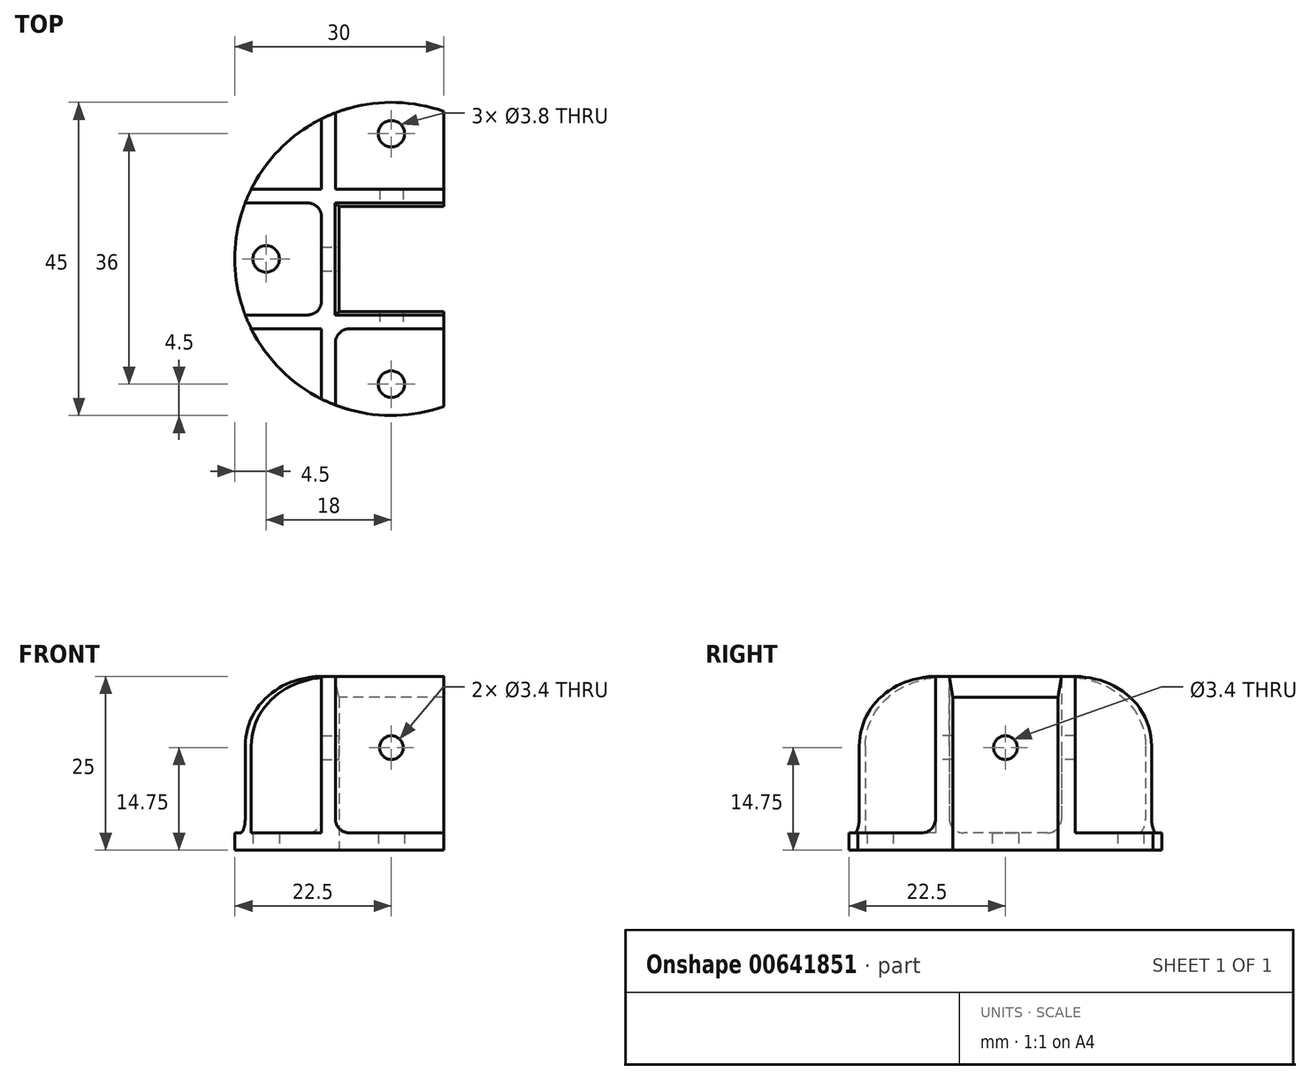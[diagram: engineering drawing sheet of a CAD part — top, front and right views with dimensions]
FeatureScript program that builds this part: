
annotation { "Feature Type Name" : "Feature", "Feature Type Description" : "" }
export const myFeature = defineFeature(function(context is Context, id is Id, definition is map)
    precondition{}
    {
        {
            var Q0;
            Q0=qCreatedBy(makeId("Top.planeOp"),FACE);
            var sketch = newSketch(context, id + "F0", { "sketchPlane" : qUnion([Q0])});
            skLineSegment(sketch, "E0.bottom", {"start": v(-7.55, 7.55) * mm, "end": v(7.55, 7.55) * mm});
            skLineSegment(sketch, "E0.top", {"start": v(-7.55, -7.55) * mm, "end": v(7.55, -7.55) * mm});
            skLineSegment(sketch, "E0.left", {"start": v(-7.55, 7.55) * mm, "end": v(-7.55, -7.55) * mm});
            skLineSegment(sketch, "E0.right", {"start": v(7.55, 7.55) * mm, "end": v(7.55, -7.55) * mm});
            skCircle(sketch, "E1", {"center": v(-18, 0) * mm, "radius": 1.9 * mm});
            skCircle(sketch, "E2", {"center": v(0, 18) * mm, "radius": 1.9 * mm});
            skCircle(sketch, "E3", {"center": v(18, 0) * mm, "radius": 1.9 * mm});
            skPoint(sketch, "E3.centerSnap0", {"position": v(10.05, 0) * mm});
            skCircle(sketch, "E4", {"center": v(0, -18) * mm, "radius": 1.9 * mm});
            skCircle(sketch, "E5", {"center": v(0, 0) * mm, "radius": 22.5 * mm});
            skSolve(sketch);
        }
        {
            var Q0;
            Q0=makeQuery(id+"F0.imprint","IMPRINT",FACE,{"disambiguationData":[TD([[makeQuery(id+"F0.imprint","IMPRINT",EDGE,{"derivedFrom":sQuery(id+"F0.wireOp",EDGE,"E0.bottom")}),1.0]])]});
            extrude(context, id + "F1", {"entities" : qUnion([Q0]), "depth" : 2.5 * mm, "offsetDistance" : 25 * mm});
        }
        {
            var Q0;
            Q0=makeQuery(id+"F1.opExtrude","CAP_FACE",FACE,{"disambiguationData":[OSD([sQuery(id+"F0.wireOp",EDGE,"E0.bottom"),sQuery(id+"F0.wireOp",EDGE,"E0.top"),sQuery(id+"F0.wireOp",EDGE,"E0.left"),sQuery(id+"F0.wireOp",EDGE,"E0.right"),sQuery(id+"F0.wireOp",EDGE,"E1"),sQuery(id+"F0.wireOp",EDGE,"E2"),sQuery(id+"F0.wireOp",EDGE,"E3"),sQuery(id+"F0.wireOp",EDGE,"E4"),sQuery(id+"F0.wireOp",EDGE,"E5")])],"isStart":false});
            var sketch = newSketch(context, id + "F2", { "sketchPlane" : qUnion([Q0])});
            skLineSegment(sketch, "E6.bottom", {"start": v(-7.55, 7.55) * mm, "end": v(7.55, 7.55) * mm});
            skLineSegment(sketch, "E6.top", {"start": v(-7.55, -7.55) * mm, "end": v(7.55, -7.55) * mm});
            skLineSegment(sketch, "E6.left", {"start": v(-7.55, 7.55) * mm, "end": v(-7.55, -7.55) * mm});
            skLineSegment(sketch, "E6.right", {"start": v(7.55, 7.55) * mm, "end": v(7.55, -7.55) * mm});
            skLineSegment(sketch, "E7.bottom", {"start": v(-10.05, 10.05) * mm, "end": v(10.05, 10.05) * mm});
            skLineSegment(sketch, "E7.top", {"start": v(-10.05, -10.05) * mm, "end": v(10.05, -10.05) * mm});
            skLineSegment(sketch, "E7.left", {"start": v(-10.05, 10.05) * mm, "end": v(-10.05, -10.05) * mm});
            skLineSegment(sketch, "E7.right", {"start": v(10.05, 10.05) * mm, "end": v(10.05, -10.05) * mm});
            skSolve(sketch);
        }
        {
            var Q0;
            Q0=makeQuery(id+"F2.imprint","IMPRINT",FACE,{"disambiguationData":[TD([[makeQuery(id+"F2.imprint","IMPRINT",EDGE,{"derivedFrom":sQuery(id+"F2.wireOp",EDGE,"E6.bottom")}),1.0]])]});
            extrude(context, id + "F3", {"entities" : qUnion([Q0]), "operationType" : NewBodyOperationType.ADD, "depth" : 22.5 * mm, "offsetDistance" : 25 * mm});
        }
        {
            var Q0;
            Q0=makeQuery(id+"F1.opExtrude","CAP_FACE",FACE,{"disambiguationData":[OSD([sQuery(id+"F0.wireOp",EDGE,"E0.bottom"),sQuery(id+"F0.wireOp",EDGE,"E0.top"),sQuery(id+"F0.wireOp",EDGE,"E0.left"),sQuery(id+"F0.wireOp",EDGE,"E0.right"),sQuery(id+"F0.wireOp",EDGE,"E1"),sQuery(id+"F0.wireOp",EDGE,"E2"),sQuery(id+"F0.wireOp",EDGE,"E3"),sQuery(id+"F0.wireOp",EDGE,"E4"),sQuery(id+"F0.wireOp",EDGE,"E5")])],"isStart":false});
            var sketch = newSketch(context, id + "F4", { "sketchPlane" : qUnion([Q0])});
            skLineSegment(sketch, "E8", {"start": v(-10.05, -10.05) * mm, "end": v(-20.13, -10.05) * mm});
            skLineSegment(sketch, "E9", {"start": v(-10.05, -10.05) * mm, "end": v(-10.05, -20.13) * mm});
            skLineSegment(sketch, "E10", {"start": v(-10.05, 10.05) * mm, "end": v(-10.05, 20.13) * mm});
            skLineSegment(sketch, "E11", {"start": v(-10.05, 10.05) * mm, "end": v(-20.13, 10.05) * mm});
            skLineSegment(sketch, "E12", {"start": v(10.05, 10.05) * mm, "end": v(10.05, 20.13) * mm});
            skLineSegment(sketch, "E13", {"start": v(10.05, 10.05) * mm, "end": v(20.13, 10.05) * mm});
            skLineSegment(sketch, "E14", {"start": v(10.05, -10.05) * mm, "end": v(20.13, -10.05) * mm});
            skLineSegment(sketch, "E15", {"start": v(10.05, -10.05) * mm, "end": v(10.05, -20.13) * mm});
            skLineSegment(sketch, "E16", {"start": v(-10.05, -10.05) * mm, "end": v(-10.05, -8.05) * mm});
            skLineSegment(sketch, "E17", {"start": v(-10.05, -8.05) * mm, "end": v(-21.01, -8.05) * mm});
            skArc(sketch, "E18", {"start": v(-20.13, 10.05) * mm, "mid": v(-20.6, 9.06) * mm, "end": v(-21.01, 8.05) * mm});
            skLineSegment(sketch, "E19", {"start": v(-10.05, -10.05) * mm, "end": v(-8.05, -10.05) * mm});
            skLineSegment(sketch, "E20", {"start": v(-8.05, -10.05) * mm, "end": v(-8.05, -21.01) * mm});
            skLineSegment(sketch, "E21", {"start": v(10.05, -10.05) * mm, "end": v(8.05, -10.05) * mm});
            skLineSegment(sketch, "E22", {"start": v(8.05, -10.05) * mm, "end": v(8.05, -21.01) * mm});
            skLineSegment(sketch, "E23", {"start": v(10.05, -10.05) * mm, "end": v(10.05, -8.05) * mm});
            skLineSegment(sketch, "E24", {"start": v(10.05, -8.05) * mm, "end": v(21.01, -8.05) * mm});
            skLineSegment(sketch, "E25", {"start": v(-10.05, 10.05) * mm, "end": v(-10.05, 8.05) * mm});
            skLineSegment(sketch, "E26", {"start": v(-10.05, 8.05) * mm, "end": v(-21.01, 8.05) * mm});
            skLineSegment(sketch, "E27", {"start": v(-10.05, 10.05) * mm, "end": v(-8.05, 10.05) * mm});
            skLineSegment(sketch, "E28", {"start": v(-8.05, 10.05) * mm, "end": v(-8.05, 21.01) * mm});
            skLineSegment(sketch, "E29", {"start": v(10.05, 10.05) * mm, "end": v(8.05, 10.05) * mm});
            skLineSegment(sketch, "E30", {"start": v(8.05, 10.05) * mm, "end": v(8.05, 21.01) * mm});
            skLineSegment(sketch, "E31", {"start": v(10.05, 10.05) * mm, "end": v(10.05, 8.05) * mm});
            skLineSegment(sketch, "E32", {"start": v(10.05, 8.05) * mm, "end": v(21.01, 8.05) * mm});
            skArc(sketch, "E33.trimOffspring", {"start": v(-8.05, 21.01) * mm, "mid": v(-9.06, 20.6) * mm, "end": v(-10.05, 20.13) * mm});
            skArc(sketch, "E34.trimOffspring", {"start": v(10.05, 20.13) * mm, "mid": v(9.06, 20.6) * mm, "end": v(8.05, 21.01) * mm});
            skArc(sketch, "E35.trimOffspring", {"start": v(21.01, 8.05) * mm, "mid": v(20.6, 9.06) * mm, "end": v(20.13, 10.05) * mm});
            skArc(sketch, "E36.trimOffspring", {"start": v(20.13, -10.05) * mm, "mid": v(20.6, -9.06) * mm, "end": v(21.01, -8.05) * mm});
            skArc(sketch, "E37.trimOffspring", {"start": v(-21.01, -8.05) * mm, "mid": v(-20.6, -9.06) * mm, "end": v(-20.13, -10.05) * mm});
            skArc(sketch, "E38.trimOffspring", {"start": v(-10.05, -20.13) * mm, "mid": v(-9.06, -20.6) * mm, "end": v(-8.05, -21.01) * mm});
            skArc(sketch, "E39.trimOffspring", {"start": v(8.05, -21.01) * mm, "mid": v(9.06, -20.6) * mm, "end": v(10.05, -20.13) * mm});
            skSolve(sketch);
        }
        {
            var Q0;
            Q0=makeQuery(id+"F4.imprint","IMPRINT",FACE,{"disambiguationData":[TD([[makeQuery(id+"F4.imprint","IMPRINT",EDGE,{"derivedFrom":sQuery(id+"F4.wireOp",EDGE,"E11")}),1.0]])]});
            var Q1;
            Q1=makeQuery(id+"F4.imprint","IMPRINT",FACE,{"disambiguationData":[TD([[makeQuery(id+"F4.imprint","IMPRINT",EDGE,{"derivedFrom":sQuery(id+"F4.wireOp",EDGE,"E8")}),-1.0]])]});
            var Q2;
            Q2=makeQuery(id+"F4.imprint","IMPRINT",FACE,{"disambiguationData":[TD([[makeQuery(id+"F4.imprint","IMPRINT",EDGE,{"derivedFrom":sQuery(id+"F4.wireOp",EDGE,"E9")}),1.0]])]});
            var Q3;
            Q3=makeQuery(id+"F4.imprint","IMPRINT",FACE,{"disambiguationData":[TD([[makeQuery(id+"F4.imprint","IMPRINT",EDGE,{"derivedFrom":sQuery(id+"F4.wireOp",EDGE,"E15")}),-1.0]])]});
            var Q4;
            Q4=makeQuery(id+"F4.imprint","IMPRINT",FACE,{"disambiguationData":[TD([[makeQuery(id+"F4.imprint","IMPRINT",EDGE,{"derivedFrom":sQuery(id+"F4.wireOp",EDGE,"E14")}),1.0]])]});
            var Q5;
            Q5=makeQuery(id+"F4.imprint","IMPRINT",FACE,{"disambiguationData":[TD([[makeQuery(id+"F4.imprint","IMPRINT",EDGE,{"derivedFrom":sQuery(id+"F4.wireOp",EDGE,"E13")}),-1.0]])]});
            var Q6;
            Q6=makeQuery(id+"F4.imprint","IMPRINT",FACE,{"disambiguationData":[TD([[makeQuery(id+"F4.imprint","IMPRINT",EDGE,{"derivedFrom":sQuery(id+"F4.wireOp",EDGE,"E12")}),1.0]])]});
            var Q7;
            Q7=makeQuery(id+"F4.imprint","IMPRINT",FACE,{"disambiguationData":[TD([[makeQuery(id+"F4.imprint","IMPRINT",EDGE,{"derivedFrom":sQuery(id+"F4.wireOp",EDGE,"E10")}),-1.0]])]});
            extrude(context, id + "F5", {"entities" : qUnion([Q0, Q1, Q2, Q3, Q4, Q5, Q6, Q7]), "operationType" : NewBodyOperationType.ADD, "depth" : 22.5 * mm, "offsetDistance" : 25 * mm});
        }
        {
            var Q0;
            Q0=makeQuery(id+"F5.opExtrude","CAP_EDGE",EDGE,{"disambiguationData":[OSD([sQuery(id+"F4.wireOp",EDGE,"E37.trimOffspring")])],"isStart":false});
            var Q1;
            Q1=makeQuery(id+"F5.opExtrude","CAP_EDGE",EDGE,{"disambiguationData":[OSD([sQuery(id+"F4.wireOp",EDGE,"E39.trimOffspring")])],"isStart":false});
            var Q2;
            Q2=makeQuery(id+"F5.opExtrude","CAP_EDGE",EDGE,{"disambiguationData":[OSD([sQuery(id+"F4.wireOp",EDGE,"E35.trimOffspring")])],"isStart":false});
            var Q3;
            Q3=makeQuery(id+"F5.opExtrude","CAP_EDGE",EDGE,{"disambiguationData":[OSD([sQuery(id+"F4.wireOp",EDGE,"E33.trimOffspring")])],"isStart":false});
            fillet(context, id + "F6", {"entities" : qUnion([Q0, Q1, Q2, Q3]), "radius" : 10 * mm, "tangentPropagation" : true, "allowEdgeOverflow" : false});
        }
        {
            var Q0;
            Q0=makeQuery(id+"F5.opExtrude","CAP_EDGE",EDGE,{"disambiguationData":[OSD([sQuery(id+"F4.wireOp",EDGE,"E10")])],"isStart":true});
            var Q1;
            Q1=makeQuery(id+"F5.opExtrude","SWEPT_EDGE",EDGE,{"disambiguationData":[OSD([sQuery(id+"F4.wireOp",EDGE,"E10"),sQuery(id+"F4.wireOp",EDGE,"E11"),sQuery(id+"F4.wireOp",EDGE,"E25"),sQuery(id+"F4.wireOp",EDGE,"E27")]),OD(0.0)]});
            var Q2;
            Q2=makeQuery(id+"F5.boolean.opBoolean","MERGE",EDGE,{"derivedFrom":[makeQuery(id+"F3.opExtrude","CAP_EDGE",EDGE,{"disambiguationData":[OSD([sQuery(id+"F2.wireOp",EDGE,"E7.bottom")])],"isStart":true}),makeQuery(id+"F5.opExtrude","CAP_EDGE",EDGE,{"disambiguationData":[OSD([sQuery(id+"F4.wireOp",EDGE,"E11")])],"isStart":true})]});
            fillet(context, id + "F7", {"entities" : qUnion([Q0, Q1, Q2]), "radius" : 2 * mm, "tangentPropagation" : true, "allowEdgeOverflow" : false});
        }
        {
            var Q0;
            Q0=makeQuery(id+"F5.boolean.opBoolean","MERGE",EDGE,{"disambiguationData":[OD(0.0)],"derivedFrom":[makeQuery(id+"F3.opExtrude","CAP_EDGE",EDGE,{"disambiguationData":[OSD([sQuery(id+"F2.wireOp",EDGE,"E7.left")])],"isStart":true}),makeQuery(id+"F5.opExtrude","CAP_EDGE",EDGE,{"disambiguationData":[OSD([sQuery(id+"F4.wireOp",EDGE,"E9")])],"isStart":true})]});
            var Q1;
            Q1=makeQuery(id+"F5.opExtrude","SWEPT_EDGE",EDGE,{"disambiguationData":[OSD([sQuery(id+"F4.wireOp",EDGE,"E8"),sQuery(id+"F4.wireOp",EDGE,"E9"),sQuery(id+"F4.wireOp",EDGE,"E16"),sQuery(id+"F4.wireOp",EDGE,"E19")]),OD(0.0)]});
            var Q2;
            Q2=makeQuery(id+"F5.opExtrude","CAP_EDGE",EDGE,{"disambiguationData":[OSD([sQuery(id+"F4.wireOp",EDGE,"E8")])],"isStart":true});
            fillet(context, id + "F8", {"entities" : qUnion([Q0, Q1, Q2]), "radius" : 2 * mm, "tangentPropagation" : true, "allowEdgeOverflow" : false});
        }
        {
            var Q0;
            Q0=makeQuery(id+"F3.opExtrude","CAP_EDGE",EDGE,{"disambiguationData":[OSD([sQuery(id+"F2.wireOp",EDGE,"E6.top")])],"isStart":false});
            var Q1;
            Q1=makeQuery(id+"F3.opExtrude","CAP_EDGE",EDGE,{"disambiguationData":[OSD([sQuery(id+"F2.wireOp",EDGE,"E6.left")])],"isStart":false});
            var Q2;
            Q2=makeQuery(id+"F3.opExtrude","CAP_EDGE",EDGE,{"disambiguationData":[OSD([sQuery(id+"F2.wireOp",EDGE,"E6.bottom")])],"isStart":false});
            var Q3;
            Q3=makeQuery(id+"F3.opExtrude","CAP_EDGE",EDGE,{"disambiguationData":[OSD([sQuery(id+"F2.wireOp",EDGE,"E6.right")])],"isStart":false});
            chamfer(context, id + "F9", {"entities" : qUnion([Q0, Q1, Q2, Q3]), "chamferType" : ChamferType.OFFSET_ANGLE, "width" : 3 * mm, "oppositeDirection" : false, "angle" : 10 * degree, "tangentPropagation" : true});
        }
        {
            var Q0;
            Q0=makeQuery(id+"F5.opExtrude","SWEPT_EDGE",EDGE,{"disambiguationData":[OSD([sQuery(id+"F2.wireOp",EDGE,"E7.left"),sQuery(id+"F4.wireOp",EDGE,"E25"),sQuery(id+"F4.wireOp",EDGE,"E26")])]});
            var Q1;
            Q1=makeQuery(id+"F5.opExtrude","CAP_EDGE",EDGE,{"disambiguationData":[OSD([sQuery(id+"F4.wireOp",EDGE,"E26")])],"isStart":true});
            var Q2;
            Q2=makeQuery(id+"F5.boolean.opBoolean","MERGE",EDGE,{"disambiguationData":[OD(1.0)],"derivedFrom":[makeQuery(id+"F3.opExtrude","CAP_EDGE",EDGE,{"disambiguationData":[OSD([sQuery(id+"F2.wireOp",EDGE,"E7.left")])],"isStart":true}),makeQuery(id+"F5.opExtrude","CAP_EDGE",EDGE,{"disambiguationData":[OSD([sQuery(id+"F4.wireOp",EDGE,"E9")])],"isStart":true})]});
            var Q3;
            Q3=makeQuery(id+"F5.opExtrude","SWEPT_EDGE",EDGE,{"disambiguationData":[OSD([sQuery(id+"F2.wireOp",EDGE,"E7.left"),sQuery(id+"F4.wireOp",EDGE,"E16"),sQuery(id+"F4.wireOp",EDGE,"E17")])]});
            var Q4;
            Q4=makeQuery(id+"F5.opExtrude","CAP_EDGE",EDGE,{"disambiguationData":[OSD([sQuery(id+"F4.wireOp",EDGE,"E17")])],"isStart":true});
            fillet(context, id + "F10", {"entities" : qUnion([Q0, Q1, Q2, Q3, Q4]), "radius" : 2 * mm, "tangentPropagation" : true, "allowEdgeOverflow" : false});
        }
        {
            var Q0;
            Q0=makeQuery(id+"F5.boolean.opBoolean","MERGE",FACE,{"disambiguationData":[OD(1.0)],"derivedFrom":[makeQuery(id+"F3.opExtrude","SWEPT_FACE",FACE,{"disambiguationData":[OSD([sQuery(id+"F2.wireOp",EDGE,"E7.right")])]}),makeQuery(id+"F5.opExtrude","SWEPT_FACE",FACE,{"disambiguationData":[OSD([sQuery(id+"F4.wireOp",EDGE,"E15")])]})]});
            var sketch = newSketch(context, id + "F11", { "sketchPlane" : qUnion([Q0])});
            skCircle(sketch, "E40", {"center": v(0, 14.75) * mm, "radius": 1.7 * mm});
            skPoint(sketch, "E40.centerSnap0", {"position": v(-6.05, 14.75) * mm});
            skSolve(sketch);
        }
        {
            var Q0;
            Q0=makeQuery(id+"F11.imprint","IMPRINT",FACE,{"disambiguationData":[TD([[makeQuery(id+"F11.imprint","IMPRINT",EDGE,{"derivedFrom":sQuery(id+"F11.wireOp",EDGE,"E40")}),1.0]])]});
            extrude(context, id + "F12", {"entities" : qUnion([Q0]), "operationType" : NewBodyOperationType.REMOVE, "oppositeDirection" : true, "depth" : 25 * mm, "offsetDistance" : 25 * mm});
        }
        {
            var Q0;
            Q0=makeQuery(id+"F3.opExtrude","SWEPT_FACE",FACE,{"disambiguationData":[OSD([sQuery(id+"F2.wireOp",EDGE,"E7.top")])]});
            var sketch = newSketch(context, id + "F13", { "sketchPlane" : qUnion([Q0])});
            skCircle(sketch, "E41", {"center": v(0, 14.75) * mm, "radius": 1.7 * mm});
            skPoint(sketch, "E41.centerSnap0", {"position": v(-6.05, 14.75) * mm});
            skSolve(sketch);
        }
        {
            var Q0;
            Q0=makeQuery(id+"F13.imprint","IMPRINT",FACE,{"disambiguationData":[TD([[makeQuery(id+"F13.imprint","IMPRINT",EDGE,{"derivedFrom":sQuery(id+"F13.wireOp",EDGE,"E41")}),1.0]])]});
            extrude(context, id + "F14", {"entities" : qUnion([Q0]), "operationType" : NewBodyOperationType.REMOVE, "oppositeDirection" : true, "depth" : 25 * mm, "offsetDistance" : 25 * mm});
        }
        {
            var Q0;
            {var subQ0=sQuery(id+"F0.wireOp",EDGE,"E3");var subQ1=sQuery(id+"F0.wireOp",EDGE,"E5");Q0=makeQuery(id+"F5.boolean.opBoolean","SPLIT",FACE,{"disambiguationData":[TD([makeQuery(id+"F1.opExtrude","SWEPT_FACE",FACE,{"disambiguationData":[OSD([subQ0])]})])],"derivedFrom":makeQuery(id+"F1.opExtrude","CAP_FACE",FACE,{"disambiguationData":[OSD([sQuery(id+"F0.wireOp",EDGE,"E0.bottom"),sQuery(id+"F0.wireOp",EDGE,"E0.top"),sQuery(id+"F0.wireOp",EDGE,"E0.left"),sQuery(id+"F0.wireOp",EDGE,"E0.right"),sQuery(id+"F0.wireOp",EDGE,"E1"),sQuery(id+"F0.wireOp",EDGE,"E2"),subQ0,sQuery(id+"F0.wireOp",EDGE,"E4"),subQ1])],"isStart":false})});}
            var sketch = newSketch(context, id + "F15", { "sketchPlane" : qUnion([Q0])});
            skLineSegment(sketch, "E42.bottom", {"start": v(7.5, 25) * mm, "end": v(24.02, 25) * mm});
            skLineSegment(sketch, "E42.top", {"start": v(7.5, -25) * mm, "end": v(24.02, -25) * mm});
            skLineSegment(sketch, "E42.left", {"start": v(7.5, 25) * mm, "end": v(7.5, -25) * mm});
            skLineSegment(sketch, "E42.right", {"start": v(24.02, 25) * mm, "end": v(24.02, -25) * mm});
            skSolve(sketch);
        }
        {
            var Q0;
            {var subQ2=sQuery(id+"F0.wireOp",EDGE,"E3");Q0=makeQuery(id+"F15.imprint","IMPRINT",FACE,{"disambiguationData":[TD([[makeQuery(id+"F15.imprint","IMPRINT",EDGE,{"derivedFrom":makeQuery(id+"F1.opExtrude","CAP_EDGE",EDGE,{"disambiguationData":[OSD([subQ2])],"isStart":false})}),-1.0]])]});}
            var Q1;
            Q1=makeQuery(id+"F15.imprint","IMPRINT",FACE,{"disambiguationData":[TD([[makeQuery(id+"F15.imprint","IMPRINT",EDGE,{"derivedFrom":sQuery(id+"F15.wireOp",EDGE,"E42.bottom")}),-1.0]])]});
            extrude(context, id + "F16", {"entities" : qUnion([Q0, Q1]), "operationType" : NewBodyOperationType.REMOVE, "endBound" : BoundingType.SYMMETRIC, "oppositeDirection" : true, "depth" : 50 * mm, "offsetDistance" : 25 * mm});
        }
        {
            var Q0;
            Q0=makeQuery(id+"F3.opExtrude","CAP_EDGE",EDGE,{"disambiguationData":[OSD([sQuery(id+"F2.wireOp",EDGE,"E7.top")])],"isStart":true});
            var Q1;
            Q1=makeQuery(id+"F5.opExtrude","CAP_EDGE",EDGE,{"disambiguationData":[OSD([sQuery(id+"F4.wireOp",EDGE,"E20")])],"isStart":true});
            var Q2;
            Q2=makeQuery(id+"F5.opExtrude","SWEPT_EDGE",EDGE,{"disambiguationData":[OSD([sQuery(id+"F2.wireOp",EDGE,"E7.top"),sQuery(id+"F4.wireOp",EDGE,"E19"),sQuery(id+"F4.wireOp",EDGE,"E20")])]});
            fillet(context, id + "F17", {"entities" : qUnion([Q0, Q1, Q2]), "radius" : 2 * mm, "tangentPropagation" : true, "allowEdgeOverflow" : false});
        }
        {
            var Q0;
            Q0=makeQuery(id+"F5.boolean.opBoolean","MERGE",EDGE,{"disambiguationData":[OD(1.0)],"derivedFrom":[makeQuery(id+"F3.opExtrude","CAP_EDGE",EDGE,{"disambiguationData":[OSD([sQuery(id+"F2.wireOp",EDGE,"E7.bottom")])],"isStart":true}),makeQuery(id+"F5.opExtrude","CAP_EDGE",EDGE,{"disambiguationData":[OSD([sQuery(id+"F4.wireOp",EDGE,"E11")])],"isStart":true}),makeQuery(id+"F5.opExtrude","CAP_EDGE",EDGE,{"disambiguationData":[OSD([sQuery(id+"F4.wireOp",EDGE,"E13")])],"isStart":true})]});
            var Q1;
            Q1=makeQuery(id+"F5.opExtrude","CAP_EDGE",EDGE,{"disambiguationData":[OSD([sQuery(id+"F4.wireOp",EDGE,"E28")])],"isStart":true});
            var Q2;
            Q2=makeQuery(id+"F5.opExtrude","SWEPT_EDGE",EDGE,{"disambiguationData":[OSD([sQuery(id+"F2.wireOp",EDGE,"E7.bottom"),sQuery(id+"F4.wireOp",EDGE,"E27"),sQuery(id+"F4.wireOp",EDGE,"E28")])]});
            fillet(context, id + "F18", {"entities" : qUnion([Q0, Q1, Q2]), "radius" : 2 * mm, "tangentPropagation" : true, "allowEdgeOverflow" : false});
        }
    });
